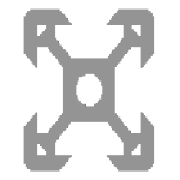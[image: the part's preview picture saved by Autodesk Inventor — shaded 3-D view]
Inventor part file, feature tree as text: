
AUTODESK INVENTOR PART (.ipt)
format: ipt  version: 2019 (Build 230136000, 136)  size: 198,656 bytes
history: native  units: mm
features: other x3, sketch x3, plane x1
ambient origin geometry x8: Origin, YZ Plane, XZ Plane, XY Plane, X Axis, Y Axis, Z Axis, Center Point
bodies: Solid1 (feature_tree), Body (feature_tree)
feature tree (7):
  other  "Driven Length"
  other  "Start Plane"
  other  "End Plane"
  sketch  "Sketch1"  dims[d2=4.2mm]
  sketch  "Sketch4"  dims[d3=1.5mm]
  plane  "Work Plane4"
  sketch  "Sketch5"  dims[d4=1.64mm d5=1.8mm d6=5.68mm d7=1.8mm d9=1.5mm d12=-0.0mm d13=470.0mm d14=0.13mm d15=0.0mm d18=90.0deg d17=470.0mm]
